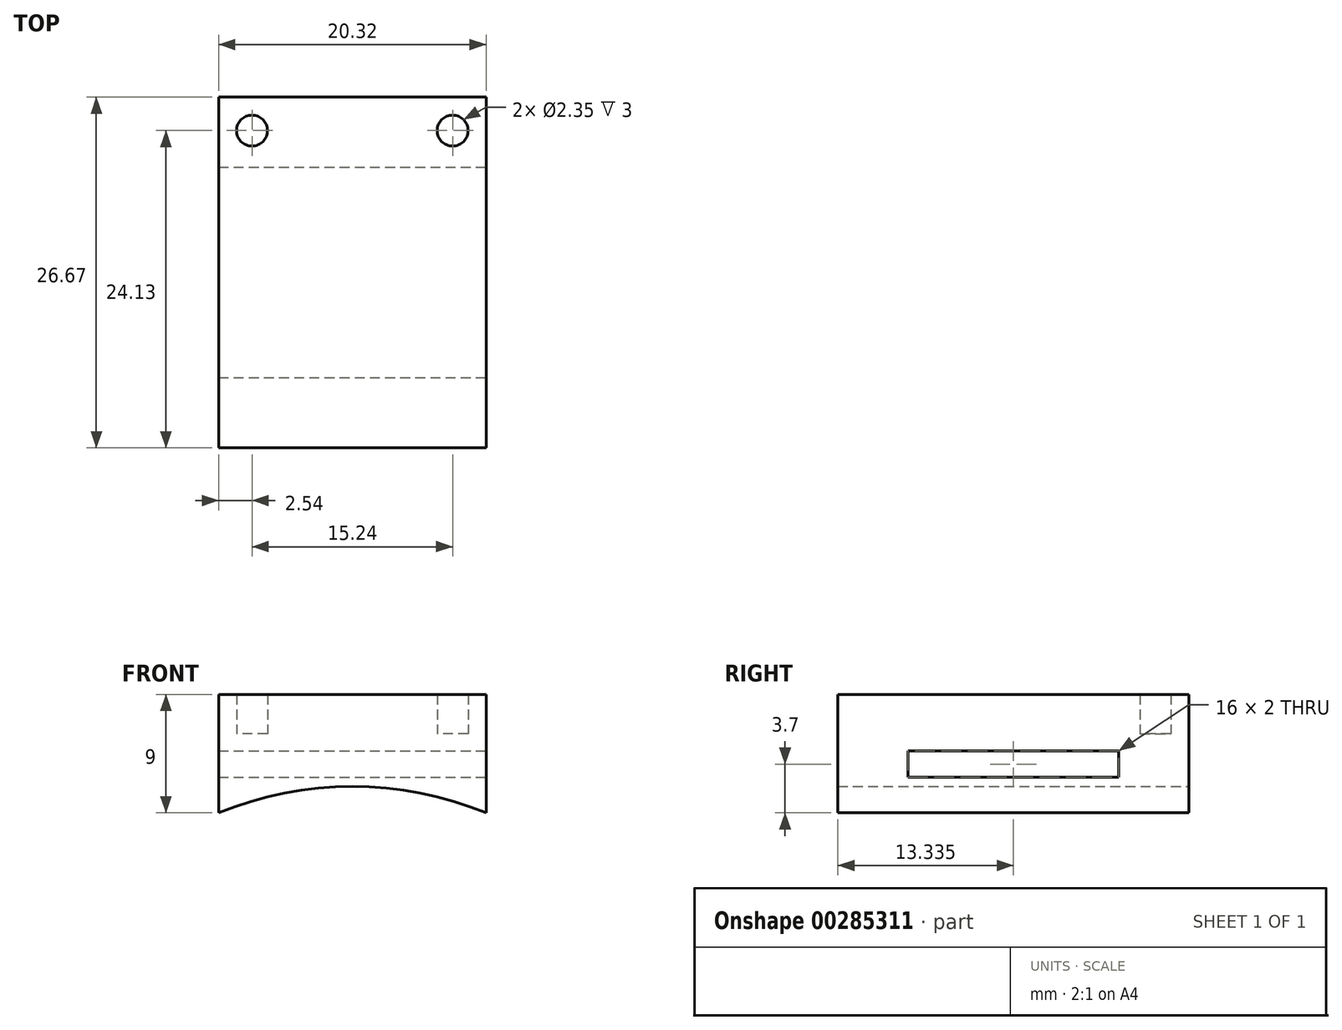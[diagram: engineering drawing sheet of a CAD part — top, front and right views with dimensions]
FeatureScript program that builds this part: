
annotation { "Feature Type Name" : "Feature", "Feature Type Description" : "" }
export const myFeature = defineFeature(function(context is Context, id is Id, definition is map)
    precondition{}
    {
        {
            var Q0;
            Q0=qCreatedBy(makeId("Front.planeOp"),FACE);
            var sketch = newSketch(context, id + "F0", { "sketchPlane" : qUnion([Q0])});
            skLineSegment(sketch, "E0.rect.bottom", {"start": v(10.16, -3.7) * mm, "end": v(-10.16, -3.7) * mm});
            skLineSegment(sketch, "E0.rect.top", {"start": v(10.16, 2.3) * mm, "end": v(-10.16, 2.3) * mm});
            skLineSegment(sketch, "E0.rect.left", {"start": v(10.16, -3.7) * mm, "end": v(10.16, 2.3) * mm});
            skLineSegment(sketch, "E0.rect.right", {"start": v(-10.16, -3.7) * mm, "end": v(-10.16, 2.3) * mm});
            skPoint(sketch, "E0.rect.middle", {"position": v(0, 0) * mm});
            skArc(sketch, "E1", {"start": v(10.16, -3.7) * mm, "mid": v(0, -1.7) * mm, "end": v(-10.16, -3.7) * mm});
            skPoint(sketch, "E2", {"position": v(0, -1.7) * mm});
            skPoint(sketch, "E3", {"position": v(0, -3.7) * mm});
            skLineSegment(sketch, "E4", {"start": v(-10.16, 0) * mm, "end": v(10.16, 0) * mm, "construction": true});
            skSolve(sketch);
        }
        {
            var Q0;
            Q0=makeQuery(id+"F0.imprint","IMPRINT",FACE,{"disambiguationData":[TD([[makeQuery(id+"F0.imprint","IMPRINT",EDGE,{"derivedFrom":sQuery(id+"F0.wireOp",EDGE,"E0.rect.top")}),1.0]])]});
            extrude(context, id + "F1", {"entities" : qUnion([Q0]), "depth" : 26.67 * mm});
        }
        {
            var Q0;
            Q0=makeQuery(id+"F1.opExtrude","SWEPT_FACE",FACE,{"disambiguationData":[OSD([sQuery(id+"F0.wireOp",EDGE,"E0.rect.left")])]});
            var sketch = newSketch(context, id + "F2", { "sketchPlane" : qUnion([Q0])});
            skLineSegment(sketch, "E5.bottom", {"start": v(-21.34, 1) * mm, "end": v(-5.34, 1) * mm});
            skLineSegment(sketch, "E5.top", {"start": v(-21.34, -1) * mm, "end": v(-5.34, -1) * mm});
            skLineSegment(sketch, "E5.left", {"start": v(-21.34, 1) * mm, "end": v(-21.34, -1) * mm});
            skLineSegment(sketch, "E5.right", {"start": v(-5.34, 1) * mm, "end": v(-5.34, -1) * mm});
            skLineSegment(sketch, "E6", {"start": v(0, 0) * mm, "end": v(-26.67, 0) * mm, "construction": true});
            skLineSegment(sketch, "E7", {"start": v(-21.34, -1) * mm, "end": v(-5.34, 1) * mm, "construction": true});
            skPoint(sketch, "E8", {"position": v(-13.34, 0) * mm});
            skSolve(sketch);
        }
        {
            var Q0;
            Q0=makeQuery(id+"F2.imprint","IMPRINT",FACE,{"disambiguationData":[TD([[makeQuery(id+"F2.imprint","IMPRINT",EDGE,{"derivedFrom":sQuery(id+"F2.wireOp",EDGE,"E5.bottom")}),-1.0]])]});
            extrude(context, id + "F3", {"entities" : qUnion([Q0]), "operationType" : NewBodyOperationType.REMOVE, "endBound" : BoundingType.UP_TO_NEXT, "oppositeDirection" : true, "depth" : 16 * mm});
        }
        {
            var Q0;
            Q0=makeQuery(id+"F1.opExtrude","SWEPT_FACE",FACE,{"disambiguationData":[OSD([sQuery(id+"F0.wireOp",EDGE,"E0.rect.top")])]});
            var sketch = newSketch(context, id + "F4", { "sketchPlane" : qUnion([Q0])});
            skLineSegment(sketch, "E9", {"start": v(-10.16, -24.13) * mm, "end": v(10.16, -24.13) * mm, "construction": true});
            skLineSegment(sketch, "E10", {"start": v(-7.62, -26.67) * mm, "end": v(-7.62, 0) * mm, "construction": true});
            skLineSegment(sketch, "E11", {"start": v(7.62, -26.67) * mm, "end": v(7.62, 0) * mm, "construction": true});
            skLineSegment(sketch, "E12", {"start": v(7.62, 0) * mm, "end": v(-7.62, -26.67) * mm, "construction": true});
            skPoint(sketch, "E13", {"position": v(0, -13.33) * mm});
            skCircle(sketch, "E14", {"center": v(-7.62, -24.13) * mm, "radius": 1.18 * mm});
            skCircle(sketch, "E15", {"center": v(7.62, -24.13) * mm, "radius": 1.18 * mm});
            skLineSegment(sketch, "E16", {"start": v(-10.16, -13.34) * mm, "end": v(10.16, -13.34) * mm, "construction": true});
            skCircle(sketch, "E17.MirrorC", {"center": v(7.62, -2.54) * mm, "radius": 1.18 * mm});
            skCircle(sketch, "E18.MirrorC", {"center": v(-7.62, -2.54) * mm, "radius": 1.18 * mm});
            skSolve(sketch);
        }
        {
            var Q0;
            Q0=makeQuery(id+"F4.imprint","IMPRINT",FACE,{"disambiguationData":[TD([[makeQuery(id+"F4.imprint","IMPRINT",EDGE,{"derivedFrom":sQuery(id+"F4.wireOp",EDGE,"E17.MirrorC")}),-1.0]])]});
            var Q1;
            Q1=makeQuery(id+"F4.imprint","IMPRINT",FACE,{"disambiguationData":[TD([[makeQuery(id+"F4.imprint","IMPRINT",EDGE,{"derivedFrom":sQuery(id+"F4.wireOp",EDGE,"E15")}),1.0]])]});
            var Q2;
            Q2=makeQuery(id+"F4.imprint","IMPRINT",FACE,{"disambiguationData":[TD([[makeQuery(id+"F4.imprint","IMPRINT",EDGE,{"derivedFrom":sQuery(id+"F4.wireOp",EDGE,"E18.MirrorC")}),-1.0]])]});
            var Q3;
            Q3=makeQuery(id+"F4.imprint","IMPRINT",FACE,{"disambiguationData":[TD([[makeQuery(id+"F4.imprint","IMPRINT",EDGE,{"derivedFrom":sQuery(id+"F4.wireOp",EDGE,"E14")}),1.0]])]});
            var Q4;
            Q4=sQuery(id+"F4.wireOp",EDGE,"E14");
            var Q5;
            Q5=sQuery(id+"F4.wireOp",EDGE,"E15");
            extrude(context, id + "F5", {"entities" : qUnion([Q0, Q1, Q2, Q3]), "operationType" : NewBodyOperationType.ADD, "surfaceEntities" : qUnion([Q4, Q5]), "depth" : 3 * mm});
        }
    });
